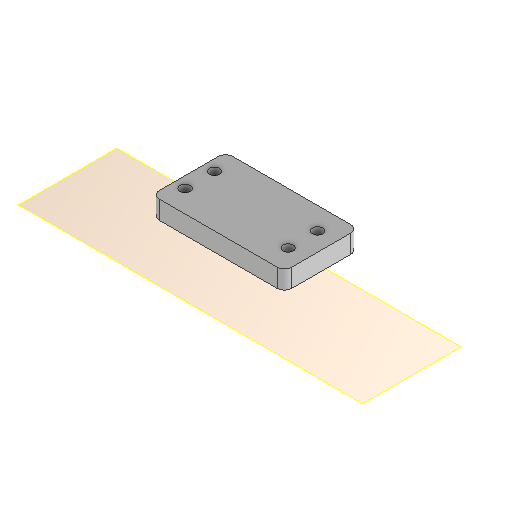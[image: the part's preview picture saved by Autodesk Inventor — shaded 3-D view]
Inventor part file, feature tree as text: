
AUTODESK INVENTOR PART (.ipt)
format: ipt  version: 2024.1 (Build 281209000, 209)  size: 122,880 bytes
history: native  units: mm
features: other x3, reference x2, plane x1, extrude x1, fillet x1, mirror x1, sketch x1
ambient origin geometry x8: Origin, YZ Plane, XZ Plane, XY Plane, X Axis, Y Axis, Z Axis, Center Point
bodies: Volumenkörper1 (feature_tree)
feature tree (10):
  plane  "Arbeitsebene1"
  extrude  "Extrusion1"  Depth=10.0mm
  fillet  "Rundung1"  Radius=3.0mm
  mirror  "Spiegeln1"
  sketch  "Skizze1"  dims[d0=36.0mm d1=10.0mm d2=3.0mm d3=5.0mm d4=0.0mm d5=2.0mm]
  reference  "Referenz1"
  reference  "Referenz2"
  other  "Assembly_Planktoscope_Uc2version_wormdrive_V3.iam"
  other  "60_Planktoscope_Base_half_wormdrive_1:2"
  other  "60_Planktoscope_Base_half1_MIR:1"
